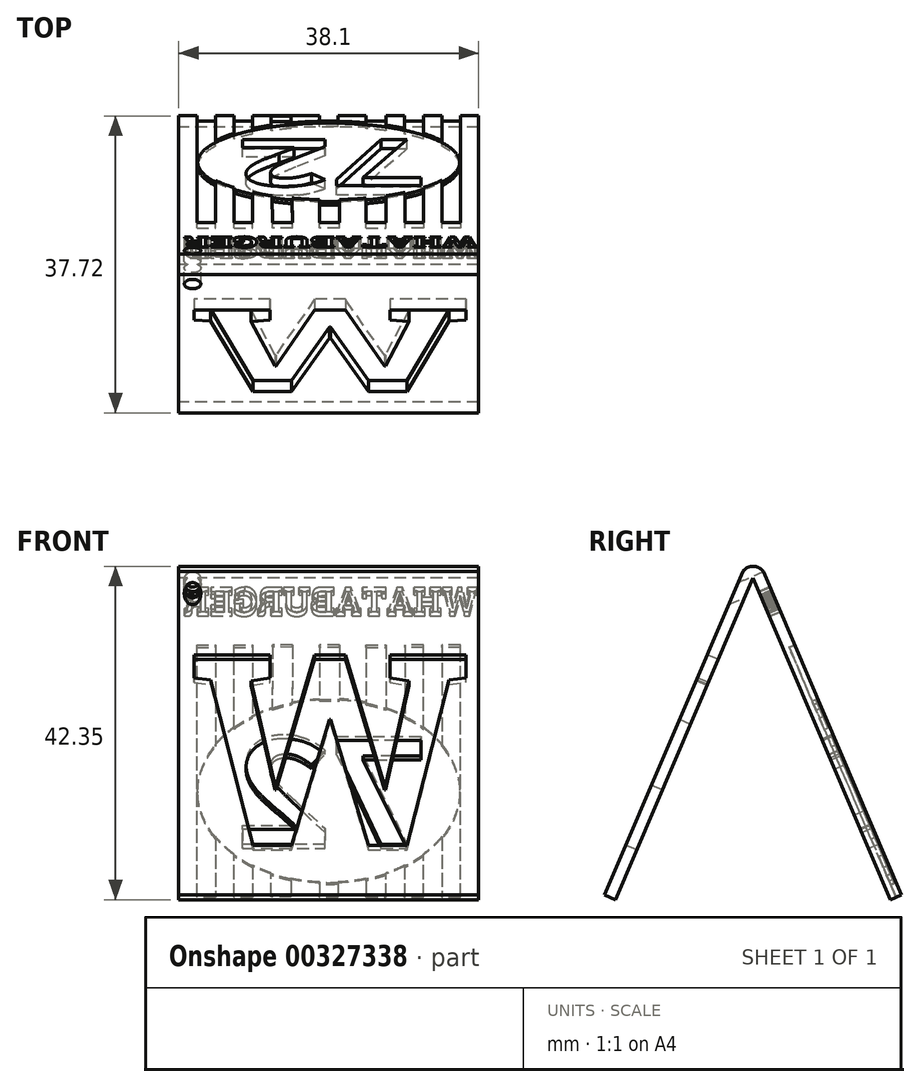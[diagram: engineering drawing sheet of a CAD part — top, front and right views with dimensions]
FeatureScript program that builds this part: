
annotation { "Feature Type Name" : "Feature", "Feature Type Description" : "" }
export const myFeature = defineFeature(function(context is Context, id is Id, definition is map)
    precondition{}
    {
        {
            var Q0;
            Q0=qCreatedBy(makeId("Right.planeOp"),FACE);
            var sketch = newSketch(context, id + "F0", { "sketchPlane" : qUnion([Q0])});
            skLineSegment(sketch, "E0", {"start": v(0, 40.88) * mm, "end": v(0, 0) * mm, "construction": true});
            skLineSegment(sketch, "E1", {"start": v(0, 40.88) * mm, "end": v(-17.46, 0) * mm});
            skLineSegment(sketch, "E2.MirrorCS", {"start": v(0, 40.88) * mm, "end": v(17.46, 0) * mm});
            skLineSegment(sketch, "E3", {"start": v(-17.46, 0) * mm, "end": v(-18.86, 0.6) * mm});
            skLineSegment(sketch, "E4", {"start": v(-18.86, 0.6) * mm, "end": v(-1.31, 41.69) * mm});
            skLineSegment(sketch, "E5.MirrorCS", {"start": v(18.86, 0.6) * mm, "end": v(1.31, 41.69) * mm});
            skLineSegment(sketch, "E6", {"start": v(18.86, 0.6) * mm, "end": v(17.46, 0) * mm});
            skLineSegment(sketch, "E7", {"start": v(0, 40.88) * mm, "end": v(0, 60.82) * mm, "construction": true});
            skPoint(sketch, "E8", {"position": v(0, 42.35) * mm});
            skArc(sketch, "E9", {"start": v(1.31, 41.69) * mm, "mid": v(0, 42.35) * mm, "end": v(-1.31, 41.69) * mm});
            skSolve(sketch);
        }
        {
            var Q0;
            Q0=makeQuery(id+"F0.imprint","IMPRINT",FACE,{"disambiguationData":[TD([[makeQuery(id+"F0.imprint","IMPRINT",EDGE,{"derivedFrom":sQuery(id+"F0.wireOp",EDGE,"E1")}),-1.0]])]});
            extrude(context, id + "F1", {"entities" : qUnion([Q0]), "depth" : 38.1 * mm});
        }
        {
            var Q0;
            Q0=makeQuery(id+"F1.opExtrude","SWEPT_FACE",FACE,{"disambiguationData":[OSD([sQuery(id+"F0.wireOp",EDGE,"E5.MirrorCS")])]});
            var sketch = newSketch(context, id + "F2", { "sketchPlane" : qUnion([Q0])});
            skEllipse(sketch, "E10", {"center": v(-19.05, 7.58) * mm, "majorRadius": 16.64 * mm, "minorRadius": 12.7 * mm, "majorAxis": v(1, 0)});
            skLineSegment(sketch, "E11", {"start": v(-35.8, -6.86) * mm, "end": v(-35.8, 27.66) * mm});
            skLineSegment(sketch, "E12", {"start": v(-35.8, 27.66) * mm, "end": v(-33.44, 27.66) * mm});
            skLineSegment(sketch, "E13", {"start": v(-33.44, 27.66) * mm, "end": v(-33.44, 13.95) * mm});
            skLineSegment(sketch, "E14", {"start": v(-33.44, 1.2) * mm, "end": v(-33.44, -6.86) * mm});
            skLineSegment(sketch, "E15", {"start": v(-33.44, -6.86) * mm, "end": v(-31.08, -6.86) * mm});
            skLineSegment(sketch, "E16", {"start": v(-31.08, -6.86) * mm, "end": v(-31.08, -1.2) * mm});
            skLineSegment(sketch, "E17", {"start": v(-31.08, 16.35) * mm, "end": v(-31.08, 27.66) * mm});
            skLineSegment(sketch, "E18", {"start": v(-31.08, 27.66) * mm, "end": v(-28.72, 27.66) * mm});
            skLineSegment(sketch, "E19", {"start": v(-28.72, 27.66) * mm, "end": v(-28.72, 17.91) * mm});
            skLineSegment(sketch, "E20", {"start": v(-28.71, -2.76) * mm, "end": v(-28.71, -6.86) * mm});
            skLineSegment(sketch, "E21", {"start": v(-28.71, -6.86) * mm, "end": v(-26.35, -6.86) * mm});
            skPoint(sketch, "E22.endSnap0", {"position": v(-2.41, 7.58) * mm});
            skLineSegment(sketch, "E23", {"start": v(-35.8, -6.86) * mm, "end": v(-33.44, -6.86) * mm});
            skLineSegment(sketch, "E24", {"start": v(-31.08, -6.86) * mm, "end": v(-28.71, -6.86) * mm});
            skLineSegment(sketch, "E25", {"start": v(-16.69, -6.86) * mm, "end": v(-14.01, -6.86) * mm});
            skLineSegment(sketch, "E26", {"start": v(-11.65, -6.86) * mm, "end": v(-9.29, -6.86) * mm});
            skLineSegment(sketch, "E27", {"start": v(-6.93, -6.86) * mm, "end": v(-4.56, -6.86) * mm});
            skLineSegment(sketch, "E28", {"start": v(-2.41, -6.86) * mm, "end": v(0, -6.86) * mm});
            skLineSegment(sketch, "E29.MirrorCS", {"start": v(-2.3, -6.86) * mm, "end": v(-2.3, 27.66) * mm});
            skLineSegment(sketch, "E30.MirrorCS", {"start": v(-4.66, 27.66) * mm, "end": v(-4.66, 13.95) * mm});
            skLineSegment(sketch, "E31.MirrorCS", {"start": v(-7.02, 16.35) * mm, "end": v(-7.02, 27.66) * mm});
            skLineSegment(sketch, "E32.MirrorCS", {"start": v(-9.38, 27.66) * mm, "end": v(-9.38, 17.91) * mm});
            skLineSegment(sketch, "E33.MirrorCS", {"start": v(-4.66, 1.2) * mm, "end": v(-4.66, -6.86) * mm});
            skLineSegment(sketch, "E34.MirrorCS", {"start": v(-7.02, -6.86) * mm, "end": v(-7.02, -1.2) * mm});
            skLineSegment(sketch, "E35.MirrorCS", {"start": v(-9.39, -2.76) * mm, "end": v(-9.39, -6.86) * mm});
            skLineSegment(sketch, "E36.MirrorCS", {"start": v(-7.02, 27.66) * mm, "end": v(-9.38, 27.66) * mm});
            skLineSegment(sketch, "E37.MirrorCS", {"start": v(-2.3, 27.66) * mm, "end": v(-4.66, 27.66) * mm});
            skLineSegment(sketch, "E38.MirrorCS", {"start": v(-2.3, -6.86) * mm, "end": v(-4.66, -6.86) * mm});
            skLineSegment(sketch, "E39.MirrorCS", {"start": v(-7.02, -6.86) * mm, "end": v(-9.39, -6.86) * mm});
            skLineSegment(sketch, "E40", {"start": v(-20.4, 27.66) * mm, "end": v(-17.87, 27.66) * mm});
            skLineSegment(sketch, "E41", {"start": v(-20.4, 27.66) * mm, "end": v(-20.4, 20.24) * mm});
            skLineSegment(sketch, "E42", {"start": v(-17.87, 27.66) * mm, "end": v(-17.87, 20.25) * mm});
            skLineSegment(sketch, "E43", {"start": v(-20.23, -5.09) * mm, "end": v(-20.23, -6.86) * mm});
            skLineSegment(sketch, "E44", {"start": v(-17.87, -5.09) * mm, "end": v(-17.87, -6.86) * mm});
            skLineSegment(sketch, "E45", {"start": v(-17.87, -6.86) * mm, "end": v(-20.23, -6.86) * mm});
            skLineSegment(sketch, "E46.MirrorCS", {"start": v(-23.82, 27.66) * mm, "end": v(-26.36, 27.66) * mm});
            skLineSegment(sketch, "E47", {"start": v(-19.14, 27.66) * mm, "end": v(-19.05, -6.86) * mm, "construction": true});
            skLineSegment(sketch, "E48.MirrorCS", {"start": v(-14.3, -4.52) * mm, "end": v(-14.29, -6.84) * mm});
            skLineSegment(sketch, "E49.MirrorCS", {"start": v(-11.75, -6.82) * mm, "end": v(-11.76, -3.8) * mm});
            skLineSegment(sketch, "E50", {"start": v(-14.29, -6.84) * mm, "end": v(-11.75, -6.82) * mm});
            skLineSegment(sketch, "E51", {"start": v(-26.36, 27.66) * mm, "end": v(-26.36, 18.99) * mm});
            skLineSegment(sketch, "E52", {"start": v(-23.82, 27.66) * mm, "end": v(-23.82, 19.75) * mm});
            skLineSegment(sketch, "E53.MirrorCS", {"start": v(-14.46, 27.69) * mm, "end": v(-14.42, 19.77) * mm});
            skLineSegment(sketch, "E54.MirrorCS", {"start": v(-14.46, 27.69) * mm, "end": v(-11.92, 27.7) * mm});
            skLineSegment(sketch, "E55.MirrorCS", {"start": v(-11.92, 27.7) * mm, "end": v(-11.88, 19.03) * mm});
            skLineSegment(sketch, "E56.MirrorCS", {"start": v(-23.81, -4.55) * mm, "end": v(-23.81, -6.86) * mm});
            skLineSegment(sketch, "E57.MirrorCS", {"start": v(-26.35, -6.86) * mm, "end": v(-26.35, -3.83) * mm});
            skLineSegment(sketch, "E58.MirrorCS", {"start": v(-23.81, -6.86) * mm, "end": v(-26.35, -6.86) * mm});
            skSolve(sketch);
        }
        {
            var Q0;
            {var subQ0=sQuery(id+"F2.wireOp",EDGE,"MmYQQPNR-c0Ji-LyPQ-T2XE-HoBNdWr0o5nU");Q0=makeQuery(id+"F2.imprint","IMPRINT",FACE,{"disambiguationData":[TD([[makeQuery(id+"F2.imprint","IMPRINT",EDGE,{"derivedFrom":subQ0}),1.0]])]});}
            var Q1;
            Q1=makeQuery(id+"F2.imprint","IMPRINT",FACE,{"disambiguationData":[TD([[makeQuery(id+"F2.imprint","IMPRINT",EDGE,{"derivedFrom":sQuery(id+"F2.wireOp",EDGE,"E11")}),-1.0]])]});
            var Q2;
            {var subQ0=sQuery(id+"F2.wireOp",EDGE,"E17");Q2=makeQuery(id+"F2.imprint","IMPRINT",FACE,{"disambiguationData":[TD([[makeQuery(id+"F2.imprint","IMPRINT",EDGE,{"derivedFrom":subQ0}),-1.0]])]});}
            var Q3;
            {var subQ0=sQuery(id+"F2.wireOp",EDGE,"hpJtBI4I-KSo4-Z8yq-gn9I-JLu5n9ADo3pZ");Q3=makeQuery(id+"F2.imprint","IMPRINT",FACE,{"disambiguationData":[TD([[makeQuery(id+"F2.imprint","IMPRINT",EDGE,{"derivedFrom":subQ0}),-1.0]])]});}
            var Q4;
            {var subQ0=sQuery(id+"F2.wireOp",EDGE,"S59L7Lo0-oiL9-fRmW-eLxj-kvCCXc1SkshM");Q4=makeQuery(id+"F2.imprint","IMPRINT",FACE,{"disambiguationData":[TD([[makeQuery(id+"F2.imprint","IMPRINT",EDGE,{"derivedFrom":subQ0}),1.0]])]});}
            var Q5;
            {var subQ0=sQuery(id+"F2.wireOp",EDGE,"yJrK0Y88-LVIV-FONG-AVv4-5vtNB8eNR7KJ");Q5=makeQuery(id+"F2.imprint","IMPRINT",FACE,{"disambiguationData":[TD([[makeQuery(id+"F2.imprint","IMPRINT",EDGE,{"derivedFrom":subQ0}),1.0]])]});}
            var Q6;
            {var subQ0=sQuery(id+"F2.wireOp",EDGE,"1oaA0eNq-0jKX-6VJy-rbbu-3H7eQxXPzSrY");Q6=makeQuery(id+"F2.imprint","IMPRINT",FACE,{"disambiguationData":[TD([[makeQuery(id+"F2.imprint","IMPRINT",EDGE,{"derivedFrom":subQ0}),1.0]])]});}
            var Q7;
            {var subQ0=sQuery(id+"F2.wireOp",EDGE,"JWuE0ec3-lRUY-hlHW-qERs-dZIE6Q2LmLep");Q7=makeQuery(id+"F2.imprint","IMPRINT",FACE,{"disambiguationData":[TD([[makeQuery(id+"F2.imprint","IMPRINT",EDGE,{"derivedFrom":subQ0}),1.0]])]});}
            var Q8;
            {var subQ0=sQuery(id+"F2.wireOp",EDGE,"iGurZPb1-gSw8-x3v7-97gH-zZSePF8nH3FV");Q8=makeQuery(id+"F2.imprint","IMPRINT",FACE,{"disambiguationData":[TD([[makeQuery(id+"F2.imprint","IMPRINT",EDGE,{"derivedFrom":subQ0}),1.0]])]});}
            var Q9;
            {var subQ0=sQuery(id+"F2.wireOp",EDGE,"SQ1tivmo-MzH2-iXoh-RoBO-uBXfkZRkDbrF");Q9=makeQuery(id+"F2.imprint","IMPRINT",FACE,{"disambiguationData":[TD([[makeQuery(id+"F2.imprint","IMPRINT",EDGE,{"derivedFrom":subQ0}),1.0]])]});}
            var Q10;
            {var subQ0=sQuery(id+"F2.wireOp",EDGE,"T3PNbqu6-gWqp-iEql-w5p1-OBcZLwCDkpuE");Q10=makeQuery(id+"F2.imprint","IMPRINT",FACE,{"disambiguationData":[TD([[makeQuery(id+"F2.imprint","IMPRINT",EDGE,{"derivedFrom":subQ0}),1.0]])]});}
            var Q11;
            {var subQ0=sQuery(id+"F2.wireOp",EDGE,"TIEQYRXC-GriU-BvMf-hB08-ezSKN2T4nnAn");Q11=makeQuery(id+"F2.imprint","IMPRINT",FACE,{"disambiguationData":[TD([[makeQuery(id+"F2.imprint","IMPRINT",EDGE,{"derivedFrom":subQ0}),-1.0]])]});}
            var Q12;
            {var subQ0=sQuery(id+"F2.wireOp",EDGE,"E16");Q12=makeQuery(id+"F2.imprint","IMPRINT",FACE,{"disambiguationData":[TD([[makeQuery(id+"F2.imprint","IMPRINT",EDGE,{"derivedFrom":subQ0}),-1.0]])]});}
            var Q13;
            {var subQ4=sQuery(id+"F2.wireOp",EDGE,"E46.MirrorCS");Q13=makeQuery(id+"F2.imprint","IMPRINT",FACE,{"disambiguationData":[TD([[makeQuery(id+"F2.imprint","IMPRINT",EDGE,{"derivedFrom":subQ4}),1.0]])]});}
            var Q14;
            {var subQ0=sQuery(id+"F2.wireOp",EDGE,"d8525b92-19d0-4a43-bd68-b3cd501098240.MirrorCS");Q14=makeQuery(id+"F2.imprint","IMPRINT",FACE,{"disambiguationData":[TD([[makeQuery(id+"F2.imprint","IMPRINT",EDGE,{"derivedFrom":subQ0}),1.0]])]});}
            var Q15;
            {var subQ0=sQuery(id+"F2.wireOp",EDGE,"E31.MirrorCS");Q15=makeQuery(id+"F2.imprint","IMPRINT",FACE,{"disambiguationData":[TD([[makeQuery(id+"F2.imprint","IMPRINT",EDGE,{"derivedFrom":subQ0}),1.0]])]});}
            var Q16;
            {var subQ2=sQuery(id+"F2.wireOp",EDGE,"E29.MirrorCS");Q16=makeQuery(id+"F2.imprint","IMPRINT",FACE,{"disambiguationData":[TD([[makeQuery(id+"F2.imprint","IMPRINT",EDGE,{"derivedFrom":subQ2}),1.0]])]});}
            var Q17;
            {var subQ0=sQuery(id+"F2.wireOp",EDGE,"E42");Q17=makeQuery(id+"F2.imprint","IMPRINT",FACE,{"disambiguationData":[TD([[makeQuery(id+"F2.imprint","IMPRINT",EDGE,{"derivedFrom":subQ0}),-1.0]])]});}
            var Q18;
            {var subQ0=sQuery(id+"F2.wireOp",EDGE,"E41");Q18=makeQuery(id+"F2.imprint","IMPRINT",FACE,{"disambiguationData":[TD([[makeQuery(id+"F2.imprint","IMPRINT",EDGE,{"derivedFrom":subQ0}),1.0]])]});}
            var Q19;
            {var subQ6=sQuery(id+"F2.wireOp",EDGE,"8e846906-1f8e-4409-8694-aef5e8dfc4d00.MirrorCS");Q19=makeQuery(id+"F2.imprint","IMPRINT",FACE,{"disambiguationData":[TD([[makeQuery(id+"F2.imprint","IMPRINT",EDGE,{"derivedFrom":subQ6}),-1.0]])]});}
            var Q20;
            {var subQ0=sQuery(id+"F2.wireOp",EDGE,"E43");Q20=makeQuery(id+"F2.imprint","IMPRINT",FACE,{"disambiguationData":[TD([[makeQuery(id+"F2.imprint","IMPRINT",EDGE,{"derivedFrom":subQ0}),1.0]])]});}
            var Q21;
            {var subQ0=sQuery(id+"F2.wireOp",EDGE,"E44");Q21=makeQuery(id+"F2.imprint","IMPRINT",FACE,{"disambiguationData":[TD([[makeQuery(id+"F2.imprint","IMPRINT",EDGE,{"derivedFrom":subQ0}),-1.0]])]});}
            var Q22;
            {var subQ0=sQuery(id+"F2.wireOp",EDGE,"1f1dcca2-fd25-4e0a-998d-8a9ba10ea2d10.MirrorCS");Q22=makeQuery(id+"F2.imprint","IMPRINT",FACE,{"disambiguationData":[TD([[makeQuery(id+"F2.imprint","IMPRINT",EDGE,{"derivedFrom":subQ0}),1.0]])]});}
            var Q23;
            {var subQ0=sQuery(id+"F2.wireOp",EDGE,"E34.MirrorCS");Q23=makeQuery(id+"F2.imprint","IMPRINT",FACE,{"disambiguationData":[TD([[makeQuery(id+"F2.imprint","IMPRINT",EDGE,{"derivedFrom":subQ0}),1.0]])]});}
            var Q24;
            {var subQ5=sQuery(id+"F2.wireOp",EDGE,"E54.MirrorCS");Q24=makeQuery(id+"F2.imprint","IMPRINT",FACE,{"disambiguationData":[TD([[makeQuery(id+"F2.imprint","IMPRINT",EDGE,{"derivedFrom":subQ5}),-1.0]])]});}
            var Q25;
            {var subQ5=sQuery(id+"F2.wireOp",EDGE,"E50");Q25=makeQuery(id+"F2.imprint","IMPRINT",FACE,{"disambiguationData":[TD([[makeQuery(id+"F2.imprint","IMPRINT",EDGE,{"derivedFrom":subQ5}),1.0]])]});}
            var Q26;
            {var subQ0=sQuery(id+"F2.wireOp",EDGE,"E57.MirrorCS");Q26=makeQuery(id+"F2.imprint","IMPRINT",FACE,{"disambiguationData":[TD([[makeQuery(id+"F2.imprint","IMPRINT",EDGE,{"derivedFrom":subQ0}),-1.0]])]});}
            extrude(context, id + "F3", {"entities" : qUnion([Q0, Q1, Q2, Q3, Q4, Q5, Q6, Q7, Q8, Q9, Q10, Q11, Q12, Q13, Q14, Q15, Q16, Q17, Q18, Q19, Q20, Q21, Q22, Q23, Q24, Q25, Q26]), "operationType" : NewBodyOperationType.REMOVE, "oppositeDirection" : true, "depth" : 0.76 * mm});
        }
        {
            var Q0;
            {var subQ19=sQuery(id+"F2.wireOp",EDGE,"E11");Q0=makeQuery(id+"F2.imprint","IMPRINT",FACE,{"disambiguationData":[TD([[makeQuery(id+"F2.imprint","IMPRINT",EDGE,{"derivedFrom":subQ19}),1.0]])]});}
            var sketch = newSketch(context, id + "F4", { "sketchPlane" : qUnion([Q0])});
            skText(sketch, "E59", { "text": "WHATABURGER", "fontName": "RobotoSlab-Bold.ttf"});
            const initialGuessF4  = {"E59": [-0.03797, 0.03231, 1, 0, 0.00338]};
            skSetInitialGuess(sketch, initialGuessF4);
            skSolve(sketch);
        }
        {
            var Q0;
            Q0 = qSketchRegion(id + "F4", true);
            extrude(context, id + "F5", {"entities" : qUnion([Q0]), "operationType" : NewBodyOperationType.REMOVE, "oppositeDirection" : true, "depth" : 2.3 * mm});
        }
        {
            var Q0;
            {var subQ0=sQuery(id+"F2.wireOp",EDGE,"E10");var subQ17=makeQuery(id+"F2.imprint","INTERSECT",VERTEX,{"derivedFrom":[subQ0,sQuery(id+"F2.wireOp",EDGE,"JWuE0ec3-lRUY-hlHW-qERs-dZIE6Q2LmLep")]});Q0=makeQuery(id+"F2.imprint","IMPRINT",FACE,{"disambiguationData":[TD([[makeQuery(id+"F2.imprint","IMPRINT",EDGE,{"disambiguationData":[TD([[subQ17,1.0]])],"derivedFrom":subQ0}),1.0]])]});}
            var sketch = newSketch(context, id + "F6", { "sketchPlane" : qUnion([Q0])});
            skText(sketch, "E60", { "text": "72", "fontName": "OpenSans-Bold.ttf"});
            const initialGuessF6  = {"E60": [-0.03135, 0.00022, 1, 0, 0.01506]};
            skSetInitialGuess(sketch, initialGuessF6);
            skSolve(sketch);
        }
        {
            var Q0;
            Q0 = qSketchRegion(id + "F6", true);
            extrude(context, id + "F7", {"entities" : qUnion([Q0]), "operationType" : NewBodyOperationType.REMOVE, "oppositeDirection" : true, "depth" : 7.62 * mm});
        }
        {
            var Q0;
            {var subQ19=sQuery(id+"F2.wireOp",EDGE,"E11");Q0=makeQuery(id+"F2.imprint","IMPRINT",FACE,{"disambiguationData":[TD([[makeQuery(id+"F2.imprint","IMPRINT",EDGE,{"derivedFrom":subQ19}),1.0]])]});}
            var sketch = newSketch(context, id + "F8", { "sketchPlane" : qUnion([Q0])});
            skCircle(sketch, "E61", {"center": v(-1.77, 36.74) * mm, "radius": 1.05 * mm});
            skSolve(sketch);
        }
        {
            var Q0;
            Q0=makeQuery(id+"F8.imprint","IMPRINT",FACE,{"disambiguationData":[TD([[makeQuery(id+"F8.imprint","IMPRINT",EDGE,{"derivedFrom":sQuery(id+"F8.wireOp",EDGE,"E61")}),1.0]])]});
            extrude(context, id + "F9", {"entities" : qUnion([Q0]), "operationType" : NewBodyOperationType.REMOVE, "oppositeDirection" : true, "depth" : 25.4 * mm});
        }
        {
            var Q0;
            Q0=makeQuery(id+"F1.opExtrude","SWEPT_FACE",FACE,{"disambiguationData":[OSD([sQuery(id+"F0.wireOp",EDGE,"E4")])]});
            var sketch = newSketch(context, id + "F10", { "sketchPlane" : qUnion([Q0])});
            skText(sketch, "E62", { "text": "W", "fontName": "RobotoSlab-Bold.ttf"});
            const initialGuessF10  = {"E62": [0.0014, 0, 1, 0, 0.02666]};
            skSetInitialGuess(sketch, initialGuessF10);
            skSolve(sketch);
        }
        {
            var Q0;
            Q0 = qSketchRegion(id + "F10", true);
            var Q1;
            Q1 = qConstructionFilter(qBodyType(qCreatedBy(id + "F10" ,EDGE), BodyType.WIRE), ConstructionObject.NO);
            extrude(context, id + "F11", {"entities" : qUnion([Q0]), "operationType" : NewBodyOperationType.REMOVE, "surfaceEntities" : qUnion([Q1]), "oppositeDirection" : true, "depth" : 7.11 * mm});
        }
        {
            var Q0;
            {var subQ0=sQuery(id+"F2.wireOp",EDGE,"E10");var subQ17=makeQuery(id+"F2.imprint","INTERSECT",VERTEX,{"derivedFrom":[subQ0,sQuery(id+"F2.wireOp",EDGE,"JWuE0ec3-lRUY-hlHW-qERs-dZIE6Q2LmLep")]});Q0=makeQuery(id+"F2.imprint","IMPRINT",FACE,{"disambiguationData":[TD([[makeQuery(id+"F2.imprint","IMPRINT",EDGE,{"disambiguationData":[TD([[subQ17,1.0]])],"derivedFrom":subQ0}),1.0]])]});}
            var Q1;
            Q1=sQuery(id+"F2.wireOp",EDGE,"E10");
            extrude(context, id + "F12", {"entities" : qUnion([Q0]), "operationType" : NewBodyOperationType.REMOVE, "surfaceEntities" : qUnion([Q1]), "oppositeDirection" : true, "depth" : 0.25 * mm});
        }
    });
